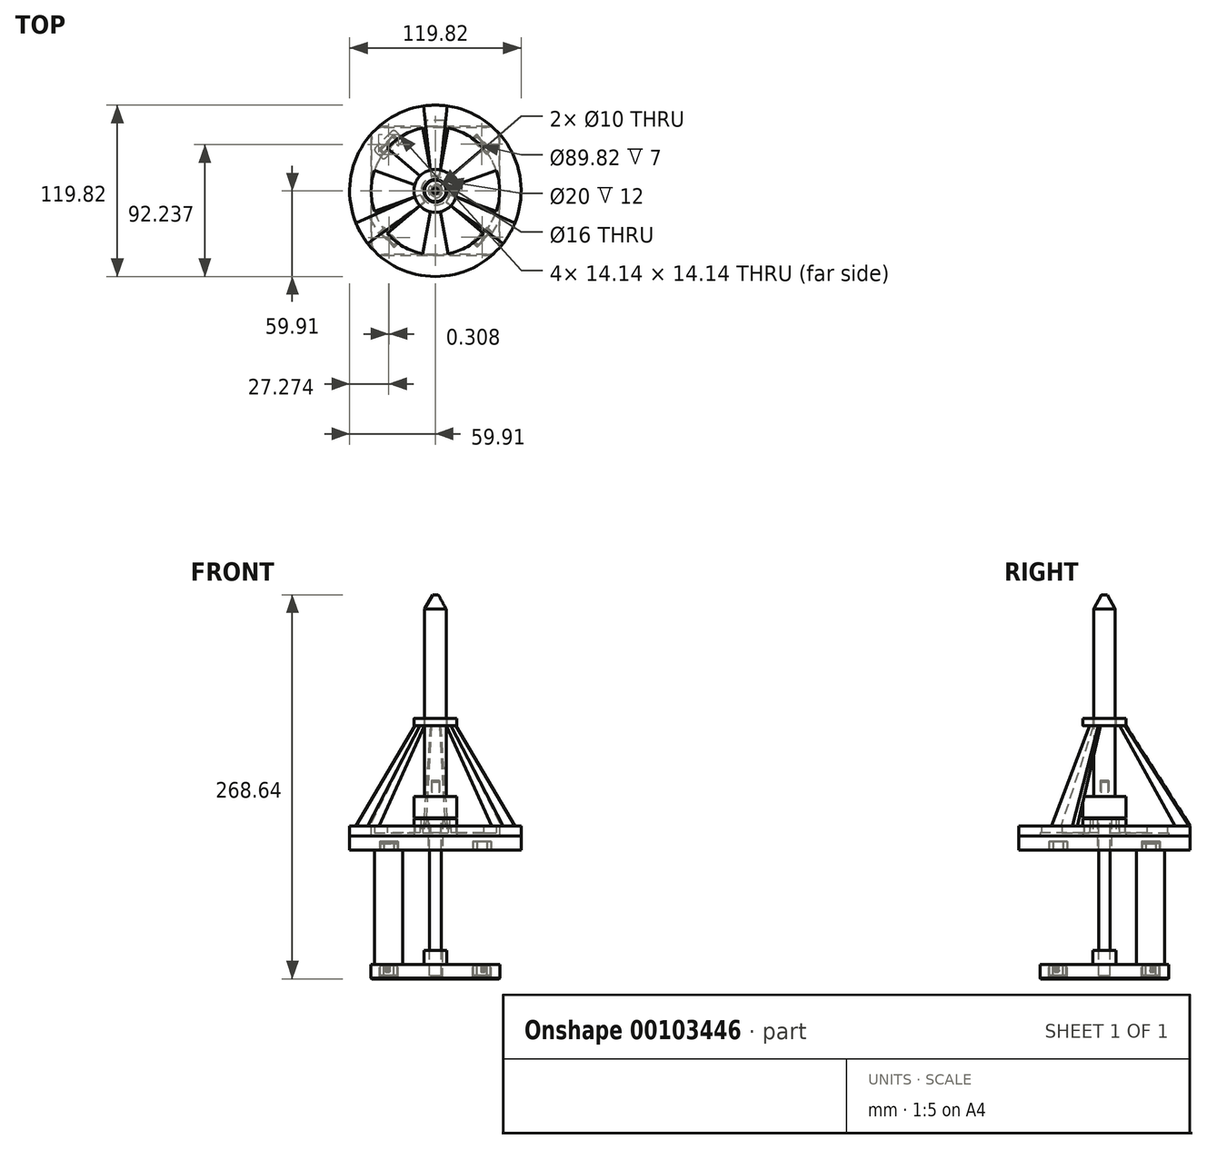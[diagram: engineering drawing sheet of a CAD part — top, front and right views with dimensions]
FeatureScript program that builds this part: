
annotation { "Feature Type Name" : "Feature", "Feature Type Description" : "" }
export const myFeature = defineFeature(function(context is Context, id is Id, definition is map)
    precondition{}
    {
        {
            var Q0;
            Q0=qCreatedBy(makeId("Top.planeOp"),FACE);
            var sketch = newSketch(context, id + "F0", { "sketchPlane" : qUnion([Q0])});
            skLineSegment(sketch, "E0.bottom", {"start": v(36, 45) * mm, "end": v(-36, 45) * mm});
            skLineSegment(sketch, "E0.top", {"start": v(36, -45) * mm, "end": v(-36, -45) * mm});
            skLineSegment(sketch, "E0.left", {"start": v(45, 36) * mm, "end": v(45, -36) * mm});
            skLineSegment(sketch, "E0.right", {"start": v(-45, 36) * mm, "end": v(-45, -36) * mm});
            skPoint(sketch, "E0.middle", {"position": v(0, 0) * mm});
            skPoint(sketch, "E1.visualSharp", {"position": v(-45, 45) * mm});
            skArc(sketch, "E1.filletArc", {"start": v(-36, 45) * mm, "mid": v(-42.36, 42.36) * mm, "end": v(-45, 36) * mm});
            skPoint(sketch, "E2.visualSharp", {"position": v(45, 45) * mm});
            skArc(sketch, "E2.filletArc", {"start": v(45, 36) * mm, "mid": v(42.36, 42.36) * mm, "end": v(36, 45) * mm});
            skPoint(sketch, "E3.visualSharp", {"position": v(45, -45) * mm});
            skArc(sketch, "E3.filletArc", {"start": v(36, -45) * mm, "mid": v(42.36, -42.36) * mm, "end": v(45, -36) * mm});
            skPoint(sketch, "E4.visualSharp", {"position": v(-45, -45) * mm});
            skArc(sketch, "E4.filletArc", {"start": v(-45, -36) * mm, "mid": v(-42.36, -42.36) * mm, "end": v(-36, -45) * mm});
            skCircle(sketch, "E5", {"center": v(0, 0) * mm, "radius": 4 * mm});
            skCircle(sketch, "E6.0", {"center": v(0, 0) * mm, "radius": 5 * mm});
            skLineSegment(sketch, "E7", {"start": v(0, 54.52) * mm, "end": v(0, -60.1) * mm, "construction": true});
            skLineSegment(sketch, "E8", {"start": v(-59, 0) * mm, "end": v(57.8, 0) * mm, "construction": true});
            skLineSegment(sketch, "E9", {"start": v(41.52, 30.51) * mm, "end": v(30.2, 41.83) * mm});
            skLineSegment(sketch, "E10", {"start": v(36, 45) * mm, "end": v(45, 36) * mm, "construction": true});
            skLineSegment(sketch, "E11", {"start": v(27.38, 41.83) * mm, "end": v(23.14, 37.59) * mm});
            skLineSegment(sketch, "E12", {"start": v(23.14, 34.76) * mm, "end": v(34.45, 23.44) * mm});
            skLineSegment(sketch, "E13", {"start": v(37.28, 23.44) * mm, "end": v(41.52, 27.69) * mm});
            skPoint(sketch, "E14.visualSharp", {"position": v(21.72, 36.17) * mm});
            skArc(sketch, "E14.filletArc", {"start": v(23.14, 37.59) * mm, "mid": v(22.55, 36.17) * mm, "end": v(23.14, 34.76) * mm});
            skPoint(sketch, "E15.visualSharp", {"position": v(28.8, 43.24) * mm});
            skArc(sketch, "E15.filletArc", {"start": v(30.2, 41.83) * mm, "mid": v(28.8, 42.41) * mm, "end": v(27.38, 41.83) * mm});
            skPoint(sketch, "E16.visualSharp", {"position": v(42.93, 29.1) * mm});
            skArc(sketch, "E16.filletArc", {"start": v(41.52, 27.69) * mm, "mid": v(42.1, 29.1) * mm, "end": v(41.52, 30.51) * mm});
            skPoint(sketch, "E17.visualSharp", {"position": v(35.86, 22.03) * mm});
            skArc(sketch, "E17.filletArc", {"start": v(34.45, 23.44) * mm, "mid": v(35.86, 22.86) * mm, "end": v(37.28, 23.44) * mm});
            skLineSegment(sketch, "E18.1.0", {"start": v(-41.83, 27.38) * mm, "end": v(-37.59, 23.14) * mm});
            skLineSegment(sketch, "E18.1.1", {"start": v(-34.76, 23.14) * mm, "end": v(-23.44, 34.45) * mm});
            skArc(sketch, "E18.1.2", {"start": v(-27.69, 41.52) * mm, "mid": v(-29.1, 42.1) * mm, "end": v(-30.51, 41.52) * mm});
            skArc(sketch, "E18.1.3", {"start": v(-37.59, 23.14) * mm, "mid": v(-36.17, 22.55) * mm, "end": v(-34.76, 23.14) * mm});
            skPoint(sketch, "E18.1.4", {"position": v(-36.17, 21.72) * mm});
            skPoint(sketch, "E18.1.5", {"position": v(-43.24, 28.8) * mm});
            skLineSegment(sketch, "E18.1.6", {"start": v(-30.51, 41.52) * mm, "end": v(-41.83, 30.2) * mm});
            skArc(sketch, "E18.1.7", {"start": v(-23.44, 34.45) * mm, "mid": v(-22.86, 35.86) * mm, "end": v(-23.44, 37.28) * mm});
            skArc(sketch, "E18.1.8", {"start": v(-41.83, 30.2) * mm, "mid": v(-42.41, 28.8) * mm, "end": v(-41.83, 27.38) * mm});
            skLineSegment(sketch, "E18.1.9", {"start": v(-23.44, 37.28) * mm, "end": v(-27.69, 41.52) * mm});
            skPoint(sketch, "E18.1.10", {"position": v(-22.03, 35.86) * mm});
            skPoint(sketch, "E18.1.11", {"position": v(-29.1, 42.93) * mm});
            skLineSegment(sketch, "E18.2.0", {"start": v(-27.38, -41.83) * mm, "end": v(-23.14, -37.59) * mm});
            skLineSegment(sketch, "E18.2.1", {"start": v(-23.14, -34.76) * mm, "end": v(-34.45, -23.44) * mm});
            skArc(sketch, "E18.2.2", {"start": v(-41.52, -27.69) * mm, "mid": v(-42.1, -29.1) * mm, "end": v(-41.52, -30.51) * mm});
            skArc(sketch, "E18.2.3", {"start": v(-23.14, -37.59) * mm, "mid": v(-22.55, -36.17) * mm, "end": v(-23.14, -34.76) * mm});
            skPoint(sketch, "E18.2.4", {"position": v(-21.72, -36.17) * mm});
            skPoint(sketch, "E18.2.5", {"position": v(-28.8, -43.24) * mm});
            skLineSegment(sketch, "E18.2.6", {"start": v(-41.52, -30.51) * mm, "end": v(-30.2, -41.83) * mm});
            skArc(sketch, "E18.2.7", {"start": v(-34.45, -23.44) * mm, "mid": v(-35.86, -22.86) * mm, "end": v(-37.28, -23.44) * mm});
            skArc(sketch, "E18.2.8", {"start": v(-30.2, -41.83) * mm, "mid": v(-28.8, -42.41) * mm, "end": v(-27.38, -41.83) * mm});
            skLineSegment(sketch, "E18.2.9", {"start": v(-37.28, -23.44) * mm, "end": v(-41.52, -27.69) * mm});
            skPoint(sketch, "E18.2.10", {"position": v(-35.86, -22.03) * mm});
            skPoint(sketch, "E18.2.11", {"position": v(-42.93, -29.1) * mm});
            skLineSegment(sketch, "E18.3.0", {"start": v(41.83, -27.38) * mm, "end": v(37.59, -23.14) * mm});
            skLineSegment(sketch, "E18.3.1", {"start": v(34.76, -23.14) * mm, "end": v(23.44, -34.45) * mm});
            skArc(sketch, "E18.3.2", {"start": v(27.69, -41.52) * mm, "mid": v(29.1, -42.1) * mm, "end": v(30.51, -41.52) * mm});
            skArc(sketch, "E18.3.3", {"start": v(37.59, -23.14) * mm, "mid": v(36.17, -22.55) * mm, "end": v(34.76, -23.14) * mm});
            skPoint(sketch, "E18.3.4", {"position": v(36.17, -21.72) * mm});
            skPoint(sketch, "E18.3.5", {"position": v(43.24, -28.8) * mm});
            skLineSegment(sketch, "E18.3.6", {"start": v(30.51, -41.52) * mm, "end": v(41.83, -30.2) * mm});
            skArc(sketch, "E18.3.7", {"start": v(23.44, -34.45) * mm, "mid": v(22.86, -35.86) * mm, "end": v(23.44, -37.28) * mm});
            skArc(sketch, "E18.3.8", {"start": v(41.83, -30.2) * mm, "mid": v(42.41, -28.8) * mm, "end": v(41.83, -27.38) * mm});
            skLineSegment(sketch, "E18.3.9", {"start": v(23.44, -37.28) * mm, "end": v(27.69, -41.52) * mm});
            skPoint(sketch, "E18.3.10", {"position": v(22.03, -35.86) * mm});
            skPoint(sketch, "E18.3.11", {"position": v(29.1, -42.93) * mm});
            skLineSegment(sketch, "E19.0", {"start": v(-36.17, 25.96) * mm, "end": v(-26.27, 35.86) * mm});
            skLineSegment(sketch, "E19.1", {"start": v(-39, 28.8) * mm, "end": v(-36.17, 25.96) * mm});
            skLineSegment(sketch, "E19.2", {"start": v(-29.1, 38.7) * mm, "end": v(-39, 28.8) * mm});
            skLineSegment(sketch, "E19.3", {"start": v(-26.27, 35.86) * mm, "end": v(-29.1, 38.7) * mm});
            skLineSegment(sketch, "E20.1.0", {"start": v(-35.86, -26.27) * mm, "end": v(-38.7, -29.1) * mm});
            skLineSegment(sketch, "E20.1.1", {"start": v(-38.7, -29.1) * mm, "end": v(-28.8, -39) * mm});
            skLineSegment(sketch, "E20.1.2", {"start": v(-25.96, -36.17) * mm, "end": v(-35.86, -26.27) * mm});
            skLineSegment(sketch, "E20.1.3", {"start": v(-28.8, -39) * mm, "end": v(-25.96, -36.17) * mm});
            skLineSegment(sketch, "E20.2.0", {"start": v(26.27, -35.86) * mm, "end": v(29.1, -38.7) * mm});
            skLineSegment(sketch, "E20.2.1", {"start": v(29.1, -38.7) * mm, "end": v(39, -28.8) * mm});
            skLineSegment(sketch, "E20.2.2", {"start": v(36.17, -25.96) * mm, "end": v(26.27, -35.86) * mm});
            skLineSegment(sketch, "E20.2.3", {"start": v(39, -28.8) * mm, "end": v(36.17, -25.96) * mm});
            skLineSegment(sketch, "E20.3.0", {"start": v(35.86, 26.27) * mm, "end": v(38.7, 29.1) * mm});
            skLineSegment(sketch, "E20.3.1", {"start": v(38.7, 29.1) * mm, "end": v(28.8, 39) * mm});
            skLineSegment(sketch, "E20.3.2", {"start": v(25.96, 36.17) * mm, "end": v(35.86, 26.27) * mm});
            skLineSegment(sketch, "E20.3.3", {"start": v(28.8, 39) * mm, "end": v(25.96, 36.17) * mm});
            skLineSegment(sketch, "E21.0", {"start": v(-29.1, 38.27) * mm, "end": v(-38.58, 28.8) * mm});
            skLineSegment(sketch, "E21.1", {"start": v(-26.7, 35.86) * mm, "end": v(-29.1, 38.27) * mm});
            skLineSegment(sketch, "E21.2", {"start": v(-36.17, 26.39) * mm, "end": v(-26.7, 35.86) * mm});
            skLineSegment(sketch, "E21.3", {"start": v(-38.58, 28.8) * mm, "end": v(-36.17, 26.39) * mm});
            skLineSegment(sketch, "E22.1.0", {"start": v(-38.27, -29.1) * mm, "end": v(-28.8, -38.58) * mm});
            skLineSegment(sketch, "E22.1.1", {"start": v(-28.8, -38.58) * mm, "end": v(-26.39, -36.17) * mm});
            skLineSegment(sketch, "E22.1.2", {"start": v(-26.39, -36.17) * mm, "end": v(-35.86, -26.7) * mm});
            skLineSegment(sketch, "E22.1.3", {"start": v(-35.86, -26.7) * mm, "end": v(-38.27, -29.1) * mm});
            skLineSegment(sketch, "E22.2.0", {"start": v(29.1, -38.27) * mm, "end": v(38.58, -28.8) * mm});
            skLineSegment(sketch, "E22.2.1", {"start": v(38.58, -28.8) * mm, "end": v(36.17, -26.39) * mm});
            skLineSegment(sketch, "E22.2.2", {"start": v(36.17, -26.39) * mm, "end": v(26.7, -35.86) * mm});
            skLineSegment(sketch, "E22.2.3", {"start": v(26.7, -35.86) * mm, "end": v(29.1, -38.27) * mm});
            skLineSegment(sketch, "E22.3.0", {"start": v(38.27, 29.1) * mm, "end": v(28.8, 38.58) * mm});
            skLineSegment(sketch, "E22.3.1", {"start": v(28.8, 38.58) * mm, "end": v(26.39, 36.17) * mm});
            skLineSegment(sketch, "E22.3.2", {"start": v(26.39, 36.17) * mm, "end": v(35.86, 26.7) * mm});
            skLineSegment(sketch, "E22.3.3", {"start": v(35.86, 26.7) * mm, "end": v(38.27, 29.1) * mm});
            skCircle(sketch, "E23.0", {"center": v(0, 0) * mm, "radius": 8 * mm});
            skSolve(sketch);
        }
        {
            var Q0;
            Q0=makeQuery(id+"F0.imprint","IMPRINT",FACE,{"disambiguationData":[TD([[makeQuery(id+"F0.imprint","IMPRINT",EDGE,{"derivedFrom":sQuery(id+"F0.wireOp",EDGE,"E0.bottom")}),1.0]])]});
            var Q1;
            Q1=makeQuery(id+"F0.imprint","IMPRINT",FACE,{"disambiguationData":[TD([[makeQuery(id+"F0.imprint","IMPRINT",EDGE,{"derivedFrom":sQuery(id+"F0.wireOp",EDGE,"E18.1.0")}),1.0]])]});
            var Q2;
            Q2=makeQuery(id+"F0.imprint","IMPRINT",FACE,{"disambiguationData":[TD([[makeQuery(id+"F0.imprint","IMPRINT",EDGE,{"derivedFrom":sQuery(id+"F0.wireOp",EDGE,"E9")}),1.0]])]});
            var Q3;
            Q3=makeQuery(id+"F0.imprint","IMPRINT",FACE,{"disambiguationData":[TD([[makeQuery(id+"F0.imprint","IMPRINT",EDGE,{"derivedFrom":sQuery(id+"F0.wireOp",EDGE,"E18.2.0")}),1.0]])]});
            var Q4;
            Q4=makeQuery(id+"F0.imprint","IMPRINT",FACE,{"disambiguationData":[TD([[makeQuery(id+"F0.imprint","IMPRINT",EDGE,{"derivedFrom":sQuery(id+"F0.wireOp",EDGE,"E18.3.0")}),1.0]])]});
            var Q5;
            Q5=makeQuery(id+"F0.imprint","IMPRINT",FACE,{"disambiguationData":[TD([[makeQuery(id+"F0.imprint","IMPRINT",EDGE,{"derivedFrom":sQuery(id+"F0.wireOp",EDGE,"E6.0")}),-1.0]])]});
            extrude(context, id + "F1", {"entities" : qUnion([Q0, Q1, Q2, Q3, Q4, Q5]), "oppositeDirection" : true, "depth" : 10 * mm});
        }
        {
            var Q0;
            Q0=makeQuery(id+"F0.imprint","IMPRINT",FACE,{"disambiguationData":[TD([[makeQuery(id+"F0.imprint","IMPRINT",EDGE,{"derivedFrom":sQuery(id+"F0.wireOp",EDGE,"E21.0")}),1.0]])]});
            extrude(context, id + "F2", {"entities" : qUnion([Q0]), "oppositeDirection" : true, "depth" : 8 * mm});
        }
        {
            var Q0;
            Q0=makeQuery(id+"F0.imprint","IMPRINT",FACE,{"disambiguationData":[TD([[makeQuery(id+"F0.imprint","IMPRINT",EDGE,{"derivedFrom":sQuery(id+"F0.wireOp",EDGE,"E19.0")}),1.0]])]});
            var Q1;
            Q1=makeQuery(id+"F0.imprint","IMPRINT",FACE,{"disambiguationData":[TD([[makeQuery(id+"F0.imprint","IMPRINT",EDGE,{"derivedFrom":sQuery(id+"F0.wireOp",EDGE,"E21.0")}),1.0]])]});
            var Q2;
            Q2=makeQuery(id+"F0.imprint","IMPRINT",FACE,{"disambiguationData":[TD([[makeQuery(id+"F0.imprint","IMPRINT",EDGE,{"derivedFrom":sQuery(id+"F0.wireOp",EDGE,"E18.1.0")}),1.0]])]});
            extrude(context, id + "F3", {"entities" : qUnion([Q0, Q1, Q2]), "depth" : 80 * mm});
        }
        {
            var Q0;
            Q0=makeQuery(id+"F3.opExtrude","CAP_FACE",FACE,{"disambiguationData":[OSD([sQuery(id+"F0.wireOp",EDGE,"E18.1.0"),sQuery(id+"F0.wireOp",EDGE,"E18.1.1"),sQuery(id+"F0.wireOp",EDGE,"E18.1.2"),sQuery(id+"F0.wireOp",EDGE,"E18.1.3"),sQuery(id+"F0.wireOp",EDGE,"E18.1.6"),sQuery(id+"F0.wireOp",EDGE,"E18.1.7"),sQuery(id+"F0.wireOp",EDGE,"E18.1.8"),sQuery(id+"F0.wireOp",EDGE,"E18.1.9")])],"isStart":false});
            var sketch = newSketch(context, id + "F4", { "sketchPlane" : qUnion([Q0])});
            skLineSegment(sketch, "E24.0", {"start": v(-29.1, 38.27) * mm, "end": v(-38.58, 28.8) * mm});
            skLineSegment(sketch, "E25.0", {"start": v(-26.7, 35.86) * mm, "end": v(-29.1, 38.27) * mm});
            skLineSegment(sketch, "E26.0", {"start": v(-36.17, 26.39) * mm, "end": v(-26.7, 35.86) * mm});
            skLineSegment(sketch, "E27.0", {"start": v(-38.58, 28.8) * mm, "end": v(-36.17, 26.39) * mm});
            skSolve(sketch);
        }
        {
            var Q0;
            Q0=makeQuery(id+"F4.imprint","IMPRINT",FACE,{"disambiguationData":[TD([[makeQuery(id+"F4.imprint","IMPRINT",EDGE,{"derivedFrom":sQuery(id+"F4.wireOp",EDGE,"E24.0")}),1.0]])]});
            extrude(context, id + "F5", {"entities" : qUnion([Q0]), "operationType" : NewBodyOperationType.ADD, "depth" : 5 * mm});
        }
        {
            var Q0;
            Q0=makeQuery(id+"F2.opExtrude","CAP_FACE",FACE,{"disambiguationData":[OSD([sQuery(id+"F0.wireOp",EDGE,"E21.0"),sQuery(id+"F0.wireOp",EDGE,"E21.1"),sQuery(id+"F0.wireOp",EDGE,"E21.2"),sQuery(id+"F0.wireOp",EDGE,"E21.3")])],"isStart":false});
            var Q1;
            Q1=makeQuery(id+"F5.opExtrude","CAP_FACE",FACE,{"disambiguationData":[OSD([sQuery(id+"F4.wireOp",EDGE,"E24.0"),sQuery(id+"F4.wireOp",EDGE,"E25.0"),sQuery(id+"F4.wireOp",EDGE,"E26.0"),sQuery(id+"F4.wireOp",EDGE,"E27.0")])],"isStart":false});
            chamfer(context, id + "F6", {"entities" : qUnion([Q0, Q1]), "width" : .5 * mm, "tangentPropagation" : true});
        }
        {
            var Q0;
            Q0=makeQuery(id+"F2.opExtrude","SWEPT_FACE",FACE,{"disambiguationData":[OSD([sQuery(id+"F0.wireOp",EDGE,"E21.0")])]});
            var sketch = newSketch(context, id + "F7", { "sketchPlane" : qUnion([Q0])});
            skText(sketch, "E28", { "text": "B", "fontName": "OpenSans-Regular.ttf"});
            const initialGuessF7  = {"E28": [-0.00182, -0.00547, 1, 0, 0.00441]};
            skSetInitialGuess(sketch, initialGuessF7);
            skSolve(sketch);
        }
        {
            var Q0;
            Q0=makeQuery(id+"F7.imprint","IMPRINT",FACE,{"disambiguationData":[TD([[makeQuery(id+"F7.imprint","IMPRINT",EDGE,{"derivedFrom":sQuery(id+"F7.wireOp",EDGE,"E28.sketch_text.stroke-0")}),-1.0]])]});
            extrude(context, id + "F8", {"entities" : qUnion([Q0]), "operationType" : NewBodyOperationType.REMOVE, "oppositeDirection" : true, "depth" : 1 * mm});
        }
        {
            var Q0;
            Q0=makeQuery(id+"F2.opExtrude","SWEPT_BODY",BODY,{"disambiguationData":[OSD([sQuery(id+"F0.wireOp",EDGE,"E21.0"),sQuery(id+"F0.wireOp",EDGE,"E21.1"),sQuery(id+"F0.wireOp",EDGE,"E21.2"),sQuery(id+"F0.wireOp",EDGE,"E21.3")])]});
            var Q1;
            Q1=makeQuery(id+"F1.opExtrude","SWEPT_FACE",FACE,{"disambiguationData":[OSD([sQuery(id+"F0.wireOp",EDGE,"E6.0")])]});
            circularPattern(context, id + "F9", {"entities" : qUnion([Q0]), "axis" : qUnion([Q1]), "angle" : 90 * degree, "instanceCount" : 4});
        }
        {
            var Q0;
            Q0=makeQuery(id+"F3.opExtrude","CAP_FACE",FACE,{"disambiguationData":[OSD([sQuery(id+"F0.wireOp",EDGE,"E18.1.0"),sQuery(id+"F0.wireOp",EDGE,"E18.1.1"),sQuery(id+"F0.wireOp",EDGE,"E18.1.2"),sQuery(id+"F0.wireOp",EDGE,"E18.1.3"),sQuery(id+"F0.wireOp",EDGE,"E18.1.6"),sQuery(id+"F0.wireOp",EDGE,"E18.1.7"),sQuery(id+"F0.wireOp",EDGE,"E18.1.8"),sQuery(id+"F0.wireOp",EDGE,"E18.1.9")])],"isStart":false});
            var sketch = newSketch(context, id + "F10", { "sketchPlane" : qUnion([Q0])});
            skLineSegment(sketch, "E29.0", {"start": v(-26.27, 35.86) * mm, "end": v(-29.1, 38.7) * mm});
            skLineSegment(sketch, "E30.0", {"start": v(-36.17, 25.96) * mm, "end": v(-26.27, 35.86) * mm});
            skLineSegment(sketch, "E31.0", {"start": v(-29.1, 38.7) * mm, "end": v(-39, 28.8) * mm});
            skLineSegment(sketch, "E32.0", {"start": v(-39, 28.8) * mm, "end": v(-36.17, 25.96) * mm});
            skLineSegment(sketch, "E33.0", {"start": v(38.7, 29.1) * mm, "end": v(28.8, 39) * mm});
            skLineSegment(sketch, "E34.0", {"start": v(28.8, 39) * mm, "end": v(25.96, 36.17) * mm});
            skLineSegment(sketch, "E35.0", {"start": v(25.96, 36.17) * mm, "end": v(35.86, 26.27) * mm});
            skLineSegment(sketch, "E36.0", {"start": v(35.86, 26.27) * mm, "end": v(38.7, 29.1) * mm});
            skLineSegment(sketch, "E37.0", {"start": v(39, -28.8) * mm, "end": v(36.17, -25.96) * mm});
            skLineSegment(sketch, "E38.0", {"start": v(36.17, -25.96) * mm, "end": v(26.27, -35.86) * mm});
            skLineSegment(sketch, "E39.0", {"start": v(29.1, -38.7) * mm, "end": v(39, -28.8) * mm});
            skLineSegment(sketch, "E40.0", {"start": v(26.27, -35.86) * mm, "end": v(29.1, -38.7) * mm});
            skLineSegment(sketch, "E41.0", {"start": v(-25.96, -36.17) * mm, "end": v(-35.86, -26.27) * mm});
            skLineSegment(sketch, "E42.0", {"start": v(-35.86, -26.27) * mm, "end": v(-38.7, -29.1) * mm});
            skLineSegment(sketch, "E43.0", {"start": v(-38.7, -29.1) * mm, "end": v(-28.8, -39) * mm});
            skLineSegment(sketch, "E44.0", {"start": v(-28.8, -39) * mm, "end": v(-25.96, -36.17) * mm});
            skCircle(sketch, "E45", {"center": v(0, 0) * mm, "radius": 59.91 * mm});
            skArc(sketch, "E46.0", {"start": v(45, 36) * mm, "mid": v(42.36, 42.36) * mm, "end": v(36, 45) * mm, "construction": true});
            skCircle(sketch, "E47.0", {"center": v(0, 0) * mm, "radius": 5 * mm});
            skSolve(sketch);
        }
        {
            var Q0;
            Q0 = qSketchRegion(id + "F10", true);
            extrude(context, id + "F11", {"entities" : qUnion([Q0]), "depth" : 10 * mm});
        }
        {
            var Q0;
            Q0=makeQuery(id+"F11.opExtrude","CAP_FACE",FACE,{"disambiguationData":[OSD([sQuery(id+"F10.wireOp",EDGE,"E29.0"),sQuery(id+"F10.wireOp",EDGE,"E30.0"),sQuery(id+"F10.wireOp",EDGE,"E31.0"),sQuery(id+"F10.wireOp",EDGE,"E32.0"),sQuery(id+"F10.wireOp",EDGE,"E33.0"),sQuery(id+"F10.wireOp",EDGE,"E34.0"),sQuery(id+"F10.wireOp",EDGE,"E35.0"),sQuery(id+"F10.wireOp",EDGE,"E36.0"),sQuery(id+"F10.wireOp",EDGE,"E37.0"),sQuery(id+"F10.wireOp",EDGE,"E38.0"),sQuery(id+"F10.wireOp",EDGE,"E39.0"),sQuery(id+"F10.wireOp",EDGE,"E40.0"),sQuery(id+"F10.wireOp",EDGE,"E41.0"),sQuery(id+"F10.wireOp",EDGE,"E42.0"),sQuery(id+"F10.wireOp",EDGE,"E43.0"),sQuery(id+"F10.wireOp",EDGE,"E44.0"),sQuery(id+"F10.wireOp",EDGE,"E45"),sQuery(id+"F10.wireOp",EDGE,"E47.0")])],"isStart":false});
            var sketch = newSketch(context, id + "F12", { "sketchPlane" : qUnion([Q0])});
            skCircle(sketch, "E48.0.0", {"center": v(0, 0) * mm, "radius": 59.91 * mm});
            skLineSegment(sketch, "E49.0", {"start": v(-36.17, 25.96) * mm, "end": v(-26.27, 35.86) * mm});
            skLineSegment(sketch, "E50.0", {"start": v(-39, 28.8) * mm, "end": v(-36.17, 25.96) * mm});
            skLineSegment(sketch, "E51.0", {"start": v(-29.1, 38.7) * mm, "end": v(-39, 28.8) * mm});
            skLineSegment(sketch, "E52.0", {"start": v(-26.27, 35.86) * mm, "end": v(-29.1, 38.7) * mm});
            skLineSegment(sketch, "E53.0", {"start": v(38.7, 29.1) * mm, "end": v(28.8, 39) * mm});
            skLineSegment(sketch, "E54.0", {"start": v(28.8, 39) * mm, "end": v(25.96, 36.17) * mm});
            skLineSegment(sketch, "E55.0", {"start": v(25.96, 36.17) * mm, "end": v(35.86, 26.27) * mm});
            skLineSegment(sketch, "E56.0", {"start": v(35.86, 26.27) * mm, "end": v(38.7, 29.1) * mm});
            skLineSegment(sketch, "E57.0", {"start": v(29.1, -38.7) * mm, "end": v(39, -28.8) * mm});
            skLineSegment(sketch, "E58.0", {"start": v(39, -28.8) * mm, "end": v(36.17, -25.96) * mm});
            skLineSegment(sketch, "E59.0", {"start": v(36.17, -25.96) * mm, "end": v(26.27, -35.86) * mm});
            skLineSegment(sketch, "E60.0", {"start": v(26.27, -35.86) * mm, "end": v(29.1, -38.7) * mm});
            skLineSegment(sketch, "E61.0", {"start": v(-25.96, -36.17) * mm, "end": v(-35.86, -26.27) * mm});
            skLineSegment(sketch, "E62.0", {"start": v(-35.86, -26.27) * mm, "end": v(-38.7, -29.1) * mm});
            skLineSegment(sketch, "E63.0", {"start": v(-38.7, -29.1) * mm, "end": v(-28.8, -39) * mm});
            skLineSegment(sketch, "E64.0", {"start": v(-28.8, -39) * mm, "end": v(-25.96, -36.17) * mm});
            skSolve(sketch);
        }
        {
            var Q0;
            Q0=makeQuery(id+"F12.imprint","IMPRINT",FACE,{"disambiguationData":[TD([[makeQuery(id+"F12.imprint","IMPRINT",EDGE,{"derivedFrom":sQuery(id+"F12.wireOp",EDGE,"E57.0")}),1.0]])]});
            var Q1;
            Q1=makeQuery(id+"F12.imprint","IMPRINT",FACE,{"disambiguationData":[TD([[makeQuery(id+"F12.imprint","IMPRINT",EDGE,{"derivedFrom":sQuery(id+"F12.wireOp",EDGE,"E53.0")}),1.0]])]});
            var Q2;
            Q2=makeQuery(id+"F12.imprint","IMPRINT",FACE,{"disambiguationData":[TD([[makeQuery(id+"F12.imprint","IMPRINT",EDGE,{"derivedFrom":sQuery(id+"F12.wireOp",EDGE,"E49.0")}),1.0]])]});
            var Q3;
            Q3=makeQuery(id+"F12.imprint","IMPRINT",FACE,{"disambiguationData":[TD([[makeQuery(id+"F12.imprint","IMPRINT",EDGE,{"derivedFrom":sQuery(id+"F12.wireOp",EDGE,"E61.0")}),1.0]])]});
            extrude(context, id + "F13", {"entities" : qUnion([Q0, Q1, Q2, Q3]), "operationType" : NewBodyOperationType.ADD, "oppositeDirection" : true, "depth" : 4 * mm});
        }
        {
            var Q0;
            Q0=makeQuery(id+"F1.opExtrude","CAP_EDGE",EDGE,{"disambiguationData":[OSD([sQuery(id+"F0.wireOp",EDGE,"E20.1.2")])],"isStart":true});
            var Q1;
            Q1=makeQuery(id+"F1.opExtrude","CAP_EDGE",EDGE,{"disambiguationData":[OSD([sQuery(id+"F0.wireOp",EDGE,"E20.1.0")])],"isStart":true});
            var Q2;
            Q2=makeQuery(id+"F1.opExtrude","CAP_EDGE",EDGE,{"disambiguationData":[OSD([sQuery(id+"F0.wireOp",EDGE,"E20.1.1")])],"isStart":true});
            var Q3;
            Q3=makeQuery(id+"F1.opExtrude","CAP_EDGE",EDGE,{"disambiguationData":[OSD([sQuery(id+"F0.wireOp",EDGE,"E20.1.3")])],"isStart":true});
            var Q4;
            Q4=makeQuery(id+"F1.opExtrude","CAP_EDGE",EDGE,{"disambiguationData":[OSD([sQuery(id+"F0.wireOp",EDGE,"E20.2.2")])],"isStart":true});
            var Q5;
            Q5=makeQuery(id+"F1.opExtrude","CAP_EDGE",EDGE,{"disambiguationData":[OSD([sQuery(id+"F0.wireOp",EDGE,"E20.2.0")])],"isStart":true});
            var Q6;
            Q6=makeQuery(id+"F1.opExtrude","CAP_EDGE",EDGE,{"disambiguationData":[OSD([sQuery(id+"F0.wireOp",EDGE,"E20.2.1")])],"isStart":true});
            var Q7;
            Q7=makeQuery(id+"F1.opExtrude","CAP_EDGE",EDGE,{"disambiguationData":[OSD([sQuery(id+"F0.wireOp",EDGE,"E20.2.3")])],"isStart":true});
            var Q8;
            Q8=makeQuery(id+"F1.opExtrude","CAP_EDGE",EDGE,{"disambiguationData":[OSD([sQuery(id+"F0.wireOp",EDGE,"E20.3.2")])],"isStart":true});
            var Q9;
            Q9=makeQuery(id+"F1.opExtrude","CAP_EDGE",EDGE,{"disambiguationData":[OSD([sQuery(id+"F0.wireOp",EDGE,"E20.3.0")])],"isStart":true});
            var Q10;
            Q10=makeQuery(id+"F1.opExtrude","CAP_EDGE",EDGE,{"disambiguationData":[OSD([sQuery(id+"F0.wireOp",EDGE,"E20.3.1")])],"isStart":true});
            var Q11;
            Q11=makeQuery(id+"F1.opExtrude","CAP_EDGE",EDGE,{"disambiguationData":[OSD([sQuery(id+"F0.wireOp",EDGE,"E20.3.3")])],"isStart":true});
            var Q12;
            Q12=makeQuery(id+"F1.opExtrude","CAP_EDGE",EDGE,{"disambiguationData":[OSD([sQuery(id+"F0.wireOp",EDGE,"E19.0")])],"isStart":true});
            var Q13;
            Q13=makeQuery(id+"F1.opExtrude","CAP_EDGE",EDGE,{"disambiguationData":[OSD([sQuery(id+"F0.wireOp",EDGE,"E19.2")])],"isStart":true});
            var Q14;
            Q14=makeQuery(id+"F1.opExtrude","CAP_EDGE",EDGE,{"disambiguationData":[OSD([sQuery(id+"F0.wireOp",EDGE,"E19.1")])],"isStart":true});
            var Q15;
            Q15=makeQuery(id+"F1.opExtrude","CAP_EDGE",EDGE,{"disambiguationData":[OSD([sQuery(id+"F0.wireOp",EDGE,"E19.3")])],"isStart":true});
            var Q16;
            Q16=makeQuery(id+"F11.opExtrude","CAP_EDGE",EDGE,{"disambiguationData":[OSD([sQuery(id+"F10.wireOp",EDGE,"E30.0")])],"isStart":true});
            var Q17;
            Q17=makeQuery(id+"F11.opExtrude","CAP_EDGE",EDGE,{"disambiguationData":[OSD([sQuery(id+"F10.wireOp",EDGE,"E31.0")])],"isStart":true});
            var Q18;
            Q18=makeQuery(id+"F11.opExtrude","CAP_EDGE",EDGE,{"disambiguationData":[OSD([sQuery(id+"F10.wireOp",EDGE,"E29.0")])],"isStart":true});
            var Q19;
            Q19=makeQuery(id+"F11.opExtrude","CAP_EDGE",EDGE,{"disambiguationData":[OSD([sQuery(id+"F10.wireOp",EDGE,"E32.0")])],"isStart":true});
            var Q20;
            Q20=makeQuery(id+"F11.opExtrude","CAP_EDGE",EDGE,{"disambiguationData":[OSD([sQuery(id+"F10.wireOp",EDGE,"E41.0")])],"isStart":true});
            var Q21;
            Q21=makeQuery(id+"F11.opExtrude","CAP_EDGE",EDGE,{"disambiguationData":[OSD([sQuery(id+"F10.wireOp",EDGE,"E43.0")])],"isStart":true});
            var Q22;
            Q22=makeQuery(id+"F11.opExtrude","CAP_EDGE",EDGE,{"disambiguationData":[OSD([sQuery(id+"F10.wireOp",EDGE,"E42.0")])],"isStart":true});
            var Q23;
            Q23=makeQuery(id+"F11.opExtrude","CAP_EDGE",EDGE,{"disambiguationData":[OSD([sQuery(id+"F10.wireOp",EDGE,"E44.0")])],"isStart":true});
            var Q24;
            Q24=makeQuery(id+"F11.opExtrude","CAP_EDGE",EDGE,{"disambiguationData":[OSD([sQuery(id+"F10.wireOp",EDGE,"E39.0")])],"isStart":true});
            var Q25;
            Q25=makeQuery(id+"F11.opExtrude","CAP_EDGE",EDGE,{"disambiguationData":[OSD([sQuery(id+"F10.wireOp",EDGE,"E37.0")])],"isStart":true});
            var Q26;
            Q26=makeQuery(id+"F11.opExtrude","CAP_EDGE",EDGE,{"disambiguationData":[OSD([sQuery(id+"F10.wireOp",EDGE,"E38.0")])],"isStart":true});
            var Q27;
            Q27=makeQuery(id+"F11.opExtrude","CAP_EDGE",EDGE,{"disambiguationData":[OSD([sQuery(id+"F10.wireOp",EDGE,"E40.0")])],"isStart":true});
            var Q28;
            Q28=makeQuery(id+"F11.opExtrude","CAP_EDGE",EDGE,{"disambiguationData":[OSD([sQuery(id+"F10.wireOp",EDGE,"E33.0")])],"isStart":true});
            var Q29;
            Q29=makeQuery(id+"F11.opExtrude","CAP_EDGE",EDGE,{"disambiguationData":[OSD([sQuery(id+"F10.wireOp",EDGE,"E36.0")])],"isStart":true});
            var Q30;
            Q30=makeQuery(id+"F11.opExtrude","CAP_EDGE",EDGE,{"disambiguationData":[OSD([sQuery(id+"F10.wireOp",EDGE,"E35.0")])],"isStart":true});
            var Q31;
            Q31=makeQuery(id+"F11.opExtrude","CAP_EDGE",EDGE,{"disambiguationData":[OSD([sQuery(id+"F10.wireOp",EDGE,"E34.0")])],"isStart":true});
            var Q32;
            Q32=makeQuery(id+"F1.opExtrude","CAP_EDGE",EDGE,{"disambiguationData":[OSD([sQuery(id+"F0.wireOp",EDGE,"E20.2.1")])],"isStart":false});
            var Q33;
            Q33=makeQuery(id+"F1.opExtrude","CAP_EDGE",EDGE,{"disambiguationData":[OSD([sQuery(id+"F0.wireOp",EDGE,"E20.2.3")])],"isStart":false});
            var Q34;
            Q34=makeQuery(id+"F1.opExtrude","CAP_EDGE",EDGE,{"disambiguationData":[OSD([sQuery(id+"F0.wireOp",EDGE,"E20.2.2")])],"isStart":false});
            var Q35;
            Q35=makeQuery(id+"F1.opExtrude","CAP_EDGE",EDGE,{"disambiguationData":[OSD([sQuery(id+"F0.wireOp",EDGE,"E20.2.0")])],"isStart":false});
            var Q36;
            Q36=makeQuery(id+"F1.opExtrude","CAP_EDGE",EDGE,{"disambiguationData":[OSD([sQuery(id+"F0.wireOp",EDGE,"E20.3.1")])],"isStart":false});
            var Q37;
            Q37=makeQuery(id+"F1.opExtrude","CAP_EDGE",EDGE,{"disambiguationData":[OSD([sQuery(id+"F0.wireOp",EDGE,"E20.3.0")])],"isStart":false});
            var Q38;
            Q38=makeQuery(id+"F1.opExtrude","CAP_EDGE",EDGE,{"disambiguationData":[OSD([sQuery(id+"F0.wireOp",EDGE,"E20.3.2")])],"isStart":false});
            var Q39;
            Q39=makeQuery(id+"F1.opExtrude","CAP_EDGE",EDGE,{"disambiguationData":[OSD([sQuery(id+"F0.wireOp",EDGE,"E20.3.3")])],"isStart":false});
            var Q40;
            Q40=makeQuery(id+"F1.opExtrude","CAP_EDGE",EDGE,{"disambiguationData":[OSD([sQuery(id+"F0.wireOp",EDGE,"E20.1.2")])],"isStart":false});
            var Q41;
            Q41=makeQuery(id+"F1.opExtrude","CAP_EDGE",EDGE,{"disambiguationData":[OSD([sQuery(id+"F0.wireOp",EDGE,"E20.1.3")])],"isStart":false});
            var Q42;
            Q42=makeQuery(id+"F1.opExtrude","CAP_EDGE",EDGE,{"disambiguationData":[OSD([sQuery(id+"F0.wireOp",EDGE,"E20.1.1")])],"isStart":false});
            var Q43;
            Q43=makeQuery(id+"F1.opExtrude","CAP_EDGE",EDGE,{"disambiguationData":[OSD([sQuery(id+"F0.wireOp",EDGE,"E20.1.0")])],"isStart":false});
            var Q44;
            Q44=makeQuery(id+"F1.opExtrude","CAP_EDGE",EDGE,{"disambiguationData":[OSD([sQuery(id+"F0.wireOp",EDGE,"E19.0")])],"isStart":false});
            var Q45;
            Q45=makeQuery(id+"F1.opExtrude","CAP_EDGE",EDGE,{"disambiguationData":[OSD([sQuery(id+"F0.wireOp",EDGE,"E19.3")])],"isStart":false});
            var Q46;
            Q46=makeQuery(id+"F1.opExtrude","CAP_EDGE",EDGE,{"disambiguationData":[OSD([sQuery(id+"F0.wireOp",EDGE,"E19.2")])],"isStart":false});
            var Q47;
            Q47=makeQuery(id+"F1.opExtrude","CAP_EDGE",EDGE,{"disambiguationData":[OSD([sQuery(id+"F0.wireOp",EDGE,"E19.1")])],"isStart":false});
            var Q48;
            Q48=makeQuery(id+"F1.opExtrude","CAP_EDGE",EDGE,{"disambiguationData":[OSD([sQuery(id+"F0.wireOp",EDGE,"E0.right")])],"isStart":false});
            chamfer(context, id + "F14", {"entities" : qUnion([Q0, Q1, Q2, Q3, Q4, Q5, Q6, Q7, Q8, Q9, Q10, Q11, Q12, Q13, Q14, Q15, Q16, Q17, Q18, Q19, Q20, Q21, Q22, Q23, Q24, Q25, Q26, Q27, Q28, Q29, Q30, Q31, Q32, Q33, Q34, Q35, Q36, Q37, Q38, Q39, Q40, Q41, Q42, Q43, Q44, Q45, Q46, Q47, Q48]), "width" : .5 * mm, "tangentPropagation" : true});
        }
        {
            var Q0;
            Q0=makeQuery(id+"F13.boolean.opBoolean","MERGE",FACE,{"derivedFrom":[makeQuery(id+"F11.opExtrude","CAP_FACE",FACE,{"disambiguationData":[OSD([sQuery(id+"F10.wireOp",EDGE,"E29.0"),sQuery(id+"F10.wireOp",EDGE,"E30.0"),sQuery(id+"F10.wireOp",EDGE,"E31.0"),sQuery(id+"F10.wireOp",EDGE,"E32.0"),sQuery(id+"F10.wireOp",EDGE,"E33.0"),sQuery(id+"F10.wireOp",EDGE,"E34.0"),sQuery(id+"F10.wireOp",EDGE,"E35.0"),sQuery(id+"F10.wireOp",EDGE,"E36.0"),sQuery(id+"F10.wireOp",EDGE,"E37.0"),sQuery(id+"F10.wireOp",EDGE,"E38.0"),sQuery(id+"F10.wireOp",EDGE,"E39.0"),sQuery(id+"F10.wireOp",EDGE,"E40.0"),sQuery(id+"F10.wireOp",EDGE,"E41.0"),sQuery(id+"F10.wireOp",EDGE,"E42.0"),sQuery(id+"F10.wireOp",EDGE,"E43.0"),sQuery(id+"F10.wireOp",EDGE,"E44.0"),sQuery(id+"F10.wireOp",EDGE,"E45"),sQuery(id+"F10.wireOp",EDGE,"E47.0")])],"isStart":false}),makeQuery(id+"F13.opExtrude","CAP_FACE",FACE,{"disambiguationData":[OSD([sQuery(id+"F12.wireOp",EDGE,"E49.0"),sQuery(id+"F12.wireOp",EDGE,"E50.0"),sQuery(id+"F12.wireOp",EDGE,"E51.0"),sQuery(id+"F12.wireOp",EDGE,"E52.0")])],"isStart":true}),makeQuery(id+"F13.opExtrude","CAP_FACE",FACE,{"disambiguationData":[OSD([sQuery(id+"F12.wireOp",EDGE,"E53.0"),sQuery(id+"F12.wireOp",EDGE,"E54.0"),sQuery(id+"F12.wireOp",EDGE,"E55.0"),sQuery(id+"F12.wireOp",EDGE,"E56.0")])],"isStart":true}),makeQuery(id+"F13.opExtrude","CAP_FACE",FACE,{"disambiguationData":[OSD([sQuery(id+"F12.wireOp",EDGE,"E57.0"),sQuery(id+"F12.wireOp",EDGE,"E58.0"),sQuery(id+"F12.wireOp",EDGE,"E59.0"),sQuery(id+"F12.wireOp",EDGE,"E60.0")])],"isStart":true}),makeQuery(id+"F13.opExtrude","CAP_FACE",FACE,{"disambiguationData":[OSD([sQuery(id+"F12.wireOp",EDGE,"E61.0"),sQuery(id+"F12.wireOp",EDGE,"E62.0"),sQuery(id+"F12.wireOp",EDGE,"E63.0"),sQuery(id+"F12.wireOp",EDGE,"E64.0")])],"isStart":true})]});
            var sketch = newSketch(context, id + "F15", { "sketchPlane" : qUnion([Q0])});
            skCircle(sketch, "E65.0", {"center": v(0, 0) * mm, "radius": 59.91 * mm});
            skCircle(sketch, "E66.0", {"center": v(0, 0) * mm, "radius": 5 * mm});
            skArc(sketch, "E67.0", {"start": v(-8.95, 44.01) * mm, "mid": v(-22.46, 38.9) * mm, "end": v(-33.64, 29.76) * mm});
            skArc(sketch, "E68.0", {"start": v(-3.63, 14.55) * mm, "mid": v(-7.5, 13) * mm, "end": v(-10.8, 10.42) * mm});
            skLineSegment(sketch, "E69", {"start": v(0, 74.9) * mm, "end": v(0, -85.15) * mm, "construction": true});
            skLineSegment(sketch, "E70", {"start": v(-3.63, 14.55) * mm, "end": v(-8.95, 44.01) * mm});
            skLineSegment(sketch, "E71.MirrorCS", {"start": v(3.63, 14.55) * mm, "end": v(8.95, 44.01) * mm});
            skLineSegment(sketch, "E72.1.0", {"start": v(-14.42, 4.14) * mm, "end": v(-42.59, 14.25) * mm});
            skLineSegment(sketch, "E72.1.1", {"start": v(-10.8, 10.42) * mm, "end": v(-33.64, 29.76) * mm});
            skLineSegment(sketch, "E72.2.0", {"start": v(-10.8, -10.42) * mm, "end": v(-33.64, -29.76) * mm});
            skLineSegment(sketch, "E72.2.1", {"start": v(-14.42, -4.14) * mm, "end": v(-42.59, -14.25) * mm});
            skLineSegment(sketch, "E72.3.0", {"start": v(3.63, -14.55) * mm, "end": v(8.95, -44.01) * mm});
            skLineSegment(sketch, "E72.3.1", {"start": v(-3.63, -14.55) * mm, "end": v(-8.95, -44.01) * mm});
            skLineSegment(sketch, "E72.4.0", {"start": v(14.42, -4.14) * mm, "end": v(42.59, -14.25) * mm});
            skLineSegment(sketch, "E72.4.1", {"start": v(10.8, -10.42) * mm, "end": v(33.64, -29.76) * mm});
            skLineSegment(sketch, "E72.5.0", {"start": v(10.8, 10.42) * mm, "end": v(33.64, 29.76) * mm});
            skLineSegment(sketch, "E72.5.1", {"start": v(14.42, 4.14) * mm, "end": v(42.59, 14.25) * mm});
            skCircle(sketch, "E73.0", {"center": v(0, 0) * mm, "radius": 8 * mm});
            skArc(sketch, "E74.trimOffspring", {"start": v(-42.59, 14.25) * mm, "mid": v(-44.91, 0) * mm, "end": v(-42.59, -14.25) * mm});
            skArc(sketch, "E75.trimOffspring", {"start": v(-14.42, 4.14) * mm, "mid": v(-15, 0) * mm, "end": v(-14.42, -4.14) * mm});
            skArc(sketch, "E76.trimOffspring", {"start": v(-10.8, -10.42) * mm, "mid": v(-7.5, -13) * mm, "end": v(-3.63, -14.55) * mm});
            skArc(sketch, "E77.trimOffspring", {"start": v(-33.64, -29.76) * mm, "mid": v(-22.46, -38.9) * mm, "end": v(-8.95, -44.01) * mm});
            skArc(sketch, "E78.trimOffspring", {"start": v(8.95, -44.01) * mm, "mid": v(22.46, -38.9) * mm, "end": v(33.64, -29.76) * mm});
            skArc(sketch, "E79.trimOffspring", {"start": v(3.63, -14.55) * mm, "mid": v(7.5, -13) * mm, "end": v(10.8, -10.42) * mm});
            skArc(sketch, "E80.trimOffspring", {"start": v(14.42, -4.14) * mm, "mid": v(15, 0) * mm, "end": v(14.42, 4.14) * mm});
            skArc(sketch, "E81.trimOffspring", {"start": v(42.59, -14.25) * mm, "mid": v(44.91, 0) * mm, "end": v(42.59, 14.25) * mm});
            skArc(sketch, "E82.trimOffspring", {"start": v(33.64, 29.76) * mm, "mid": v(22.46, 38.9) * mm, "end": v(8.95, 44.01) * mm});
            skArc(sketch, "E83.trimOffspring", {"start": v(10.8, 10.42) * mm, "mid": v(7.5, 13) * mm, "end": v(3.63, 14.55) * mm});
            skCircle(sketch, "E84.0", {"center": v(0, 0) * mm, "radius": 10 * mm});
            skCircle(sketch, "E85", {"center": v(0, 0) * mm, "radius": 44.91 * mm});
            skCircle(sketch, "E86", {"center": v(0, 0) * mm, "radius": 15 * mm});
            skCircle(sketch, "E87", {"center": v(0, 0) * mm, "radius": 4 * mm});
            skSolve(sketch);
        }
        {
            var Q0;
            Q0=makeQuery(id+"F15.imprint","IMPRINT",FACE,{"disambiguationData":[TD([[makeQuery(id+"F15.imprint","IMPRINT",EDGE,{"derivedFrom":sQuery(id+"F15.wireOp",EDGE,"E66.0")}),-1.0]])]});
            extrude(context, id + "F16", {"entities" : qUnion([Q0]), "operationType" : NewBodyOperationType.ADD, "depth" : 12 * mm});
        }
        {
            var Q0;
            Q0=makeQuery(id+"F15.imprint","IMPRINT",FACE,{"disambiguationData":[TD([[makeQuery(id+"F15.imprint","IMPRINT",EDGE,{"derivedFrom":sQuery(id+"F15.wireOp",EDGE,"E65.0")}),1.0]])]});
            var Q1;
            Q1=makeQuery(id+"F15.imprint","IMPRINT",FACE,{"disambiguationData":[TD([[makeQuery(id+"F15.imprint","IMPRINT",EDGE,{"derivedFrom":sQuery(id+"F15.wireOp",EDGE,"E84.0")}),-1.0]])]});
            extrude(context, id + "F17", {"entities" : qUnion([Q0, Q1]), "depth" : 2 * mm});
        }
        {
            var Q0;
            Q0=makeQuery(id+"F17.opExtrude","CAP_FACE",FACE,{"disambiguationData":[OSD([sQuery(id+"F15.wireOp",EDGE,"E65.0"),sQuery(id+"F15.wireOp",EDGE,"E85")])],"isStart":false});
            var sketch = newSketch(context, id + "F18", { "sketchPlane" : qUnion([Q0])});
            skCircle(sketch, "E88.0", {"center": v(0, 0) * mm, "radius": 44.91 * mm});
            skCircle(sketch, "E89.0", {"center": v(0, 0) * mm, "radius": 59.91 * mm});
            skLineSegment(sketch, "E90.0.0", {"start": v(-33.64, -29.76) * mm, "end": v(-10.8, -10.42) * mm});
            skArc(sketch, "E90.0.1", {"start": v(-10.8, -10.42) * mm, "mid": v(-13, -7.5) * mm, "end": v(-14.42, -4.14) * mm});
            skLineSegment(sketch, "E90.0.2", {"start": v(-14.42, -4.14) * mm, "end": v(-42.59, -14.25) * mm});
            skArc(sketch, "E90.0.3", {"start": v(-42.59, -14.25) * mm, "mid": v(-38.9, -22.46) * mm, "end": v(-33.64, -29.76) * mm});
            skLineSegment(sketch, "E91.0.0", {"start": v(-42.59, 14.25) * mm, "end": v(-14.42, 4.14) * mm});
            skArc(sketch, "E91.0.1", {"start": v(-14.42, 4.14) * mm, "mid": v(-13, 7.5) * mm, "end": v(-10.8, 10.42) * mm});
            skLineSegment(sketch, "E91.0.2", {"start": v(-10.8, 10.42) * mm, "end": v(-33.64, 29.76) * mm});
            skArc(sketch, "E91.0.3", {"start": v(-33.64, 29.76) * mm, "mid": v(-38.9, 22.46) * mm, "end": v(-42.59, 14.25) * mm});
            skLineSegment(sketch, "E92.0.0", {"start": v(-8.95, 44.01) * mm, "end": v(-3.63, 14.55) * mm});
            skArc(sketch, "E92.0.1", {"start": v(-3.63, 14.55) * mm, "mid": v(0, 15) * mm, "end": v(3.63, 14.55) * mm});
            skLineSegment(sketch, "E92.0.2", {"start": v(3.63, 14.55) * mm, "end": v(8.95, 44.01) * mm});
            skArc(sketch, "E92.0.3", {"start": v(8.95, 44.01) * mm, "mid": v(0, 44.91) * mm, "end": v(-8.95, 44.01) * mm});
            skLineSegment(sketch, "E93.0.0", {"start": v(33.64, 29.76) * mm, "end": v(10.8, 10.42) * mm});
            skArc(sketch, "E93.0.1", {"start": v(10.8, 10.42) * mm, "mid": v(13, 7.5) * mm, "end": v(14.42, 4.14) * mm});
            skLineSegment(sketch, "E93.0.2", {"start": v(14.42, 4.14) * mm, "end": v(42.59, 14.25) * mm});
            skArc(sketch, "E93.0.3", {"start": v(42.59, 14.25) * mm, "mid": v(38.9, 22.46) * mm, "end": v(33.64, 29.76) * mm});
            skLineSegment(sketch, "E94.0.0", {"start": v(42.59, -14.25) * mm, "end": v(14.42, -4.14) * mm});
            skArc(sketch, "E94.0.1", {"start": v(14.42, -4.14) * mm, "mid": v(13, -7.5) * mm, "end": v(10.8, -10.42) * mm});
            skLineSegment(sketch, "E94.0.2", {"start": v(10.8, -10.42) * mm, "end": v(33.64, -29.76) * mm});
            skArc(sketch, "E94.0.3", {"start": v(33.64, -29.76) * mm, "mid": v(38.9, -22.46) * mm, "end": v(42.59, -14.25) * mm});
            skLineSegment(sketch, "E95.0.0", {"start": v(8.95, -44.01) * mm, "end": v(3.63, -14.55) * mm});
            skArc(sketch, "E95.0.1", {"start": v(3.63, -14.55) * mm, "mid": v(0, -15) * mm, "end": v(-3.63, -14.55) * mm});
            skLineSegment(sketch, "E95.0.2", {"start": v(-3.63, -14.55) * mm, "end": v(-8.95, -44.01) * mm});
            skArc(sketch, "E95.0.3", {"start": v(-8.95, -44.01) * mm, "mid": v(0, -44.91) * mm, "end": v(8.95, -44.01) * mm});
            skCircle(sketch, "E96.0", {"center": v(0, 0) * mm, "radius": 10 * mm});
            skCircle(sketch, "E97.0", {"center": v(0, 0) * mm, "radius": 15 * mm});
            skCircle(sketch, "E98.0", {"center": v(0, 0) * mm, "radius": 8 * mm});
            skCircle(sketch, "E99.0", {"center": v(0, 0) * mm, "radius": 5 * mm});
            skSolve(sketch);
        }
        {
            var Q0;
            Q0=makeQuery(id+"F18.imprint","IMPRINT",FACE,{"disambiguationData":[TD([[makeQuery(id+"F18.imprint","IMPRINT",EDGE,{"derivedFrom":sQuery(id+"F18.wireOp",EDGE,"E89.0")}),1.0]])]});
            var Q1;
            {var subQ0=sQuery(id+"F18.wireOp",EDGE,"E95.0.0");Q1=makeQuery(id+"F18.imprint","IMPRINT",FACE,{"disambiguationData":[TD([[makeQuery(id+"F18.imprint","IMPRINT",EDGE,{"derivedFrom":subQ0}),1.0]])]});}
            var Q2;
            {var subQ0=sQuery(id+"F18.wireOp",EDGE,"E90.0.0");Q2=makeQuery(id+"F18.imprint","IMPRINT",FACE,{"disambiguationData":[TD([[makeQuery(id+"F18.imprint","IMPRINT",EDGE,{"derivedFrom":subQ0}),1.0]])]});}
            var Q3;
            {var subQ0=sQuery(id+"F18.wireOp",EDGE,"E91.0.0");Q3=makeQuery(id+"F18.imprint","IMPRINT",FACE,{"disambiguationData":[TD([[makeQuery(id+"F18.imprint","IMPRINT",EDGE,{"derivedFrom":subQ0}),1.0]])]});}
            var Q4;
            {var subQ0=sQuery(id+"F18.wireOp",EDGE,"E92.0.0");Q4=makeQuery(id+"F18.imprint","IMPRINT",FACE,{"disambiguationData":[TD([[makeQuery(id+"F18.imprint","IMPRINT",EDGE,{"derivedFrom":subQ0}),1.0]])]});}
            var Q5;
            {var subQ0=sQuery(id+"F18.wireOp",EDGE,"E93.0.0");Q5=makeQuery(id+"F18.imprint","IMPRINT",FACE,{"disambiguationData":[TD([[makeQuery(id+"F18.imprint","IMPRINT",EDGE,{"derivedFrom":subQ0}),1.0]])]});}
            var Q6;
            {var subQ0=sQuery(id+"F18.wireOp",EDGE,"E94.0.0");Q6=makeQuery(id+"F18.imprint","IMPRINT",FACE,{"disambiguationData":[TD([[makeQuery(id+"F18.imprint","IMPRINT",EDGE,{"derivedFrom":subQ0}),1.0]])]});}
            var Q7;
            Q7=makeQuery(id+"F18.imprint","IMPRINT",FACE,{"disambiguationData":[TD([[makeQuery(id+"F18.imprint","IMPRINT",EDGE,{"derivedFrom":sQuery(id+"F18.wireOp",EDGE,"E96.0")}),-1.0]])]});
            extrude(context, id + "F19", {"entities" : qUnion([Q0, Q1, Q2, Q3, Q4, Q5, Q6, Q7]), "operationType" : NewBodyOperationType.ADD, "depth" : 5 * mm});
        }
        {
            var Q0;
            Q0=makeQuery(id+"F19.opExtrude","CAP_FACE",FACE,{"disambiguationData":[OSD([sQuery(id+"F18.wireOp",EDGE,"E88.0"),sQuery(id+"F18.wireOp",EDGE,"E89.0"),sQuery(id+"F18.wireOp",EDGE,"E90.0.0"),sQuery(id+"F18.wireOp",EDGE,"E90.0.2"),sQuery(id+"F18.wireOp",EDGE,"E91.0.0"),sQuery(id+"F18.wireOp",EDGE,"E91.0.2"),sQuery(id+"F18.wireOp",EDGE,"E92.0.0"),sQuery(id+"F18.wireOp",EDGE,"E92.0.2"),sQuery(id+"F18.wireOp",EDGE,"E93.0.0"),sQuery(id+"F18.wireOp",EDGE,"E93.0.2"),sQuery(id+"F18.wireOp",EDGE,"E94.0.0"),sQuery(id+"F18.wireOp",EDGE,"E94.0.2"),sQuery(id+"F18.wireOp",EDGE,"E95.0.0"),sQuery(id+"F18.wireOp",EDGE,"E95.0.2"),sQuery(id+"F18.wireOp",EDGE,"E96.0"),sQuery(id+"F18.wireOp",EDGE,"E97.0")])],"isStart":false});
            var sketch = newSketch(context, id + "F20", { "sketchPlane" : qUnion([Q0])});
            skCircle(sketch, "E100.0", {"center": v(0, 0) * mm, "radius": 10 * mm});
            skArc(sketch, "E101.0", {"start": v(-3.63, 14.55) * mm, "mid": v(-7.5, 13) * mm, "end": v(-10.8, 10.42) * mm});
            skCircle(sketch, "E102", {"center": v(0, 0) * mm, "radius": 15 * mm});
            skSolve(sketch);
        }
        {
            var Q0;
            Q0=makeQuery(id+"F20.imprint","IMPRINT",FACE,{"disambiguationData":[TD([[makeQuery(id+"F20.imprint","IMPRINT",EDGE,{"derivedFrom":sQuery(id+"F20.wireOp",EDGE,"E100.0")}),-1.0]])]});
            extrude(context, id + "F21", {"entities" : qUnion([Q0]), "operationType" : NewBodyOperationType.ADD, "depth" : 5 * mm});
        }
        {
            var Q0;
            Q0=makeQuery(id+"F15.imprint","IMPRINT",FACE,{"disambiguationData":[TD([[makeQuery(id+"F15.imprint","IMPRINT",EDGE,{"derivedFrom":sQuery(id+"F15.wireOp",EDGE,"E87")}),1.0]])]});
            var Q1;
            Q1=makeQuery(id+"F9.opPattern","COPY",FACE,{"derivedFrom":makeQuery(id+"F2.opExtrude","CAP_FACE",FACE,{"disambiguationData":[OSD([sQuery(id+"F0.wireOp",EDGE,"E21.0"),sQuery(id+"F0.wireOp",EDGE,"E21.1"),sQuery(id+"F0.wireOp",EDGE,"E21.2"),sQuery(id+"F0.wireOp",EDGE,"E21.3")])],"isStart":false}),"instanceName":"3"});
            extrude(context, id + "F22", {"entities" : qUnion([Q0]), "endBound" : BoundingType.UP_TO_SURFACE, "oppositeDirection" : true, "endBoundEntityFace" : qUnion([Q1]), "depth" : 96.72 * mm});
        }
        {
            var Q0;
            Q0=makeQuery(id+"F0.imprint","IMPRINT",FACE,{"disambiguationData":[TD([[makeQuery(id+"F0.imprint","IMPRINT",EDGE,{"derivedFrom":sQuery(id+"F0.wireOp",EDGE,"E6.0")}),-1.0]])]});
            extrude(context, id + "F23", {"entities" : qUnion([Q0]), "operationType" : NewBodyOperationType.ADD, "depth" : 10 * mm});
        }
        {
            var Q0;
            Q0=makeQuery(id+"F22.opExtrude","CAP_FACE",FACE,{"disambiguationData":[OSD([sQuery(id+"F15.wireOp",EDGE,"E87")])],"isStart":true});
            extrude(context, id + "F24", {"entities" : qUnion([Q0]), "operationType" : NewBodyOperationType.ADD, "depth" : 12.5 * mm});
        }
        {
            var Q0;
            Q0=makeQuery(id+"F24.opExtrude","CAP_FACE",FACE,{"disambiguationData":[OSD([sQuery(id+"F15.wireOp",EDGE,"E87")])],"isStart":false});
            var sketch = newSketch(context, id + "F25", { "sketchPlane" : qUnion([Q0])});
            skCircle(sketch, "E103.0", {"center": v(0, 0) * mm, "radius": 15 * mm});
            skSolve(sketch);
        }
        {
            var Q0;
            Q0=makeQuery(id+"F25.imprint","IMPRINT",FACE,{"disambiguationData":[TD([[makeQuery(id+"F25.imprint","IMPRINT",EDGE,{"derivedFrom":sQuery(id+"F25.wireOp",EDGE,"E103.0")}),1.0]])]});
            var Q1;
            Q1=makeQuery(id+"F25.imprint","IMPRINT",FACE,{"disambiguationData":[TD([[makeQuery(id+"F25.imprint","IMPRINT",EDGE,{"derivedFrom":makeQuery(id+"F24.opExtrude","CAP_EDGE",EDGE,{"disambiguationData":[OSD([sQuery(id+"F15.wireOp",EDGE,"E87")])],"isStart":false})}),1.0]])]});
            var Q2;
            Q2=sQuery(id+"F25.wireOp",EDGE,"E103.0");
            extrude(context, id + "F26", {"entities" : qUnion([Q0, Q1]), "operationType" : NewBodyOperationType.ADD, "surfaceEntities" : qUnion([Q2]), "depth" : 15 * mm});
        }
        {
            var Q0;
            Q0=makeQuery(id+"F26.opExtrude","CAP_FACE",FACE,{"disambiguationData":[OSD([sQuery(id+"F25.wireOp",EDGE,"E103.0")])],"isStart":false});
            var sketch = newSketch(context, id + "F27", { "sketchPlane" : qUnion([Q0])});
            skLineSegment(sketch, "E104.bottom", {"start": v(2.5, 2.5) * mm, "end": v(-2.5, 2.5) * mm});
            skLineSegment(sketch, "E104.top", {"start": v(2.5, -2.5) * mm, "end": v(-2.5, -2.5) * mm});
            skLineSegment(sketch, "E104.left", {"start": v(2.5, 2.5) * mm, "end": v(2.5, -2.5) * mm});
            skLineSegment(sketch, "E104.right", {"start": v(-2.5, 2.5) * mm, "end": v(-2.5, -2.5) * mm});
            skPoint(sketch, "E104.middle", {"position": v(0, 0) * mm});
            skCircle(sketch, "E105", {"center": v(0, 0) * mm, "radius": 7.5 * mm});
            skLineSegment(sketch, "E106.0", {"start": v(2.9, 2.9) * mm, "end": v(-2.9, 2.9) * mm});
            skLineSegment(sketch, "E106.1", {"start": v(2.9, 2.9) * mm, "end": v(2.9, -2.9) * mm});
            skLineSegment(sketch, "E106.2", {"start": v(2.9, -2.9) * mm, "end": v(-2.9, -2.9) * mm});
            skLineSegment(sketch, "E106.3", {"start": v(-2.9, 2.9) * mm, "end": v(-2.9, -2.9) * mm});
            skSolve(sketch);
        }
        {
            var Q0;
            Q0=makeQuery(id+"F27.imprint","IMPRINT",FACE,{"disambiguationData":[TD([[makeQuery(id+"F27.imprint","IMPRINT",EDGE,{"derivedFrom":sQuery(id+"F27.wireOp",EDGE,"E104.bottom")}),1.0]])]});
            extrude(context, id + "F28", {"entities" : qUnion([Q0]), "operationType" : NewBodyOperationType.ADD, "depth" : 10 * mm});
        }
        {
            var Q0;
            Q0=makeQuery(id+"F27.imprint","IMPRINT",FACE,{"disambiguationData":[TD([[makeQuery(id+"F27.imprint","IMPRINT",EDGE,{"derivedFrom":sQuery(id+"F27.wireOp",EDGE,"E105")}),1.0]])]});
            extrude(context, id + "F29", {"entities" : qUnion([Q0]), "depth" : 11.14 * mm});
        }
        {
            var Q0;
            Q0=makeQuery(id+"F29.opExtrude","CAP_FACE",FACE,{"disambiguationData":[OSD([sQuery(id+"F27.wireOp",EDGE,"E105"),sQuery(id+"F27.wireOp",EDGE,"E106.0"),sQuery(id+"F27.wireOp",EDGE,"E106.1"),sQuery(id+"F27.wireOp",EDGE,"E106.2"),sQuery(id+"F27.wireOp",EDGE,"E106.3")])],"isStart":false});
            var sketch = newSketch(context, id + "F30", { "sketchPlane" : qUnion([Q0])});
            skLineSegment(sketch, "E107.0", {"start": v(-2.9, 2.9) * mm, "end": v(-2.9, -2.9) * mm});
            skLineSegment(sketch, "E108.0", {"start": v(2.9, 2.9) * mm, "end": v(-2.9, 2.9) * mm});
            skLineSegment(sketch, "E109.0", {"start": v(2.9, 2.9) * mm, "end": v(2.9, -2.9) * mm});
            skLineSegment(sketch, "E110.0", {"start": v(2.9, -2.9) * mm, "end": v(-2.9, -2.9) * mm});
            skSolve(sketch);
        }
        {
            var Q0;
            Q0=makeQuery(id+"F30.imprint","IMPRINT",FACE,{"disambiguationData":[TD([[makeQuery(id+"F30.imprint","IMPRINT",EDGE,{"derivedFrom":sQuery(id+"F30.wireOp",EDGE,"E107.0")}),1.0]])]});
            var Q1;
            Q1=makeQuery(id+"F30.imprint","IMPRINT",FACE,{"disambiguationData":[TD([[makeQuery(id+"F30.imprint","IMPRINT",EDGE,{"derivedFrom":sQuery(id+"F30.wireOp",EDGE,"E107.0")}),-1.0]])]});
            extrude(context, id + "F31", {"entities" : qUnion([Q0, Q1]), "operationType" : NewBodyOperationType.ADD, "depth" : 120 * mm});
        }
        {
            var Q0;
            Q0=qCreatedBy(makeId("Right.planeOp"),FACE);
            var sketch = newSketch(context, id + "F32", { "sketchPlane" : qUnion([Q0])});
            skLineSegment(sketch, "E111.0", {"start": v(-59.91, 97) * mm, "end": v(59.91, 97) * mm});
            skLineSegment(sketch, "E112", {"start": v(0, 97) * mm, "end": v(0, 167) * mm});
            skPoint(sketch, "E112.endSnap0", {"position": v(0, 97) * mm});
            skSolve(sketch);
        }
        {
            var Q0;
            Q0=sQuery(id+"F32.wireOp",EDGE,"E112");
            var Q1;
            Q1=sQuery(id+"F32.wireOp",VERTEX,"E112.end");
            cPlane(context, id + "F33", {"entities" : qUnion([Q0, Q1]), "cplaneType" : CPlaneType.LINE_POINT, "offset" : 25 * mm, "width" : 150 * mm, "height" : 150 * mm});
        }
        {
            var Q0;
            Q0=qCreatedBy(id+"F33.planeOp",FACE);
            var sketch = newSketch(context, id + "F34", { "sketchPlane" : qUnion([Q0])});
            skCircle(sketch, "E113.0", {"center": v(0, 0) * mm, "radius": 7.5 * mm});
            skCircle(sketch, "E114.0", {"center": v(0, 0) * mm, "radius": 8 * mm});
            skCircle(sketch, "E115.0", {"center": v(0, 0) * mm, "radius": 15 * mm});
            skLineSegment(sketch, "E116", {"start": v(0, 18.17) * mm, "end": v(0, 0) * mm, "construction": true});
            skLineSegment(sketch, "E117.0", {"start": v(-8.95, 44.01) * mm, "end": v(-3.63, 14.55) * mm, "construction": true});
            skLineSegment(sketch, "E118.0", {"start": v(3.63, 14.55) * mm, "end": v(8.95, 44.01) * mm, "construction": true});
            skLineSegment(sketch, "E119", {"start": v(-3.63, 14.55) * mm, "end": v(-2.9, 10.52) * mm});
            skLineSegment(sketch, "E120", {"start": v(-2.9, 10.52) * mm, "end": v(0, 10.52) * mm});
            skLineSegment(sketch, "E121.MirrorCS", {"start": v(2.9, 10.52) * mm, "end": v(0, 10.52) * mm});
            skLineSegment(sketch, "E122.MirrorCS", {"start": v(3.63, 14.55) * mm, "end": v(2.9, 10.52) * mm});
            skLineSegment(sketch, "E123.1.0", {"start": v(-14.42, -4.14) * mm, "end": v(-10.56, -2.75) * mm});
            skLineSegment(sketch, "E123.1.1", {"start": v(-10.56, -2.75) * mm, "end": v(-9.11, -5.26) * mm});
            skLineSegment(sketch, "E123.1.2", {"start": v(-10.8, -10.42) * mm, "end": v(-7.66, -7.77) * mm});
            skLineSegment(sketch, "E123.1.3", {"start": v(-7.66, -7.77) * mm, "end": v(-9.11, -5.26) * mm});
            skLineSegment(sketch, "E123.2.0", {"start": v(10.8, -10.42) * mm, "end": v(7.66, -7.77) * mm});
            skLineSegment(sketch, "E123.2.1", {"start": v(7.66, -7.77) * mm, "end": v(9.11, -5.26) * mm});
            skLineSegment(sketch, "E123.2.2", {"start": v(14.42, -4.14) * mm, "end": v(10.56, -2.75) * mm});
            skLineSegment(sketch, "E123.2.3", {"start": v(10.56, -2.75) * mm, "end": v(9.11, -5.26) * mm});
            skSolve(sketch);
        }
        {
            var Q0;
            Q0=makeQuery(id+"F19.opExtrude","CAP_FACE",FACE,{"disambiguationData":[OSD([sQuery(id+"F18.wireOp",EDGE,"E88.0"),sQuery(id+"F18.wireOp",EDGE,"E89.0"),sQuery(id+"F18.wireOp",EDGE,"E90.0.0"),sQuery(id+"F18.wireOp",EDGE,"E90.0.2"),sQuery(id+"F18.wireOp",EDGE,"E91.0.0"),sQuery(id+"F18.wireOp",EDGE,"E91.0.2"),sQuery(id+"F18.wireOp",EDGE,"E92.0.0"),sQuery(id+"F18.wireOp",EDGE,"E92.0.2"),sQuery(id+"F18.wireOp",EDGE,"E93.0.0"),sQuery(id+"F18.wireOp",EDGE,"E93.0.2"),sQuery(id+"F18.wireOp",EDGE,"E94.0.0"),sQuery(id+"F18.wireOp",EDGE,"E94.0.2"),sQuery(id+"F18.wireOp",EDGE,"E95.0.0"),sQuery(id+"F18.wireOp",EDGE,"E95.0.2"),sQuery(id+"F18.wireOp",EDGE,"E96.0"),sQuery(id+"F18.wireOp",EDGE,"E97.0")])],"isStart":false});
            var sketch = newSketch(context, id + "F35", { "sketchPlane" : qUnion([Q0])});
            skLineSegment(sketch, "E124", {"start": v(0, 0) * mm, "end": v(0, 62.8) * mm, "construction": true});
            skPoint(sketch, "E124.endSnap0", {"position": v(0, 15) * mm});
            skLineSegment(sketch, "E125", {"start": v(-8.37, 59.32) * mm, "end": v(-6.54, 49.23) * mm});
            skLineSegment(sketch, "E126", {"start": v(-6.54, 49.23) * mm, "end": v(0, 49.23) * mm});
            skLineSegment(sketch, "E127.MirrorCS", {"start": v(6.54, 49.23) * mm, "end": v(0, 49.23) * mm});
            skLineSegment(sketch, "E128.MirrorCS", {"start": v(8.37, 59.32) * mm, "end": v(6.54, 49.23) * mm});
            skLineSegment(sketch, "E129.1.0", {"start": v(-55.56, -22.42) * mm, "end": v(-45.9, -18.95) * mm});
            skLineSegment(sketch, "E129.1.1", {"start": v(-45.9, -18.95) * mm, "end": v(-42.64, -24.62) * mm});
            skLineSegment(sketch, "E129.1.2", {"start": v(-39.37, -30.28) * mm, "end": v(-42.64, -24.62) * mm});
            skLineSegment(sketch, "E129.1.3", {"start": v(-47.2, -36.9) * mm, "end": v(-39.37, -30.28) * mm});
            skLineSegment(sketch, "E129.2.0", {"start": v(47.2, -36.9) * mm, "end": v(39.37, -30.28) * mm});
            skLineSegment(sketch, "E129.2.1", {"start": v(39.37, -30.28) * mm, "end": v(42.64, -24.62) * mm});
            skLineSegment(sketch, "E129.2.2", {"start": v(45.9, -18.95) * mm, "end": v(42.64, -24.62) * mm});
            skLineSegment(sketch, "E129.2.3", {"start": v(55.56, -22.42) * mm, "end": v(45.9, -18.95) * mm});
            skPoint(sketch, "E129.center", {"position": v(0, 0) * mm});
            skSolve(sketch);
        }
        {
            var Q1;
            {var subQ1=sQuery(id+"F34.wireOp",EDGE,"E123.1.0");Q1=makeQuery(id+"F34.imprint","IMPRINT",FACE,{"disambiguationData":[TD([[makeQuery(id+"F34.imprint","IMPRINT",EDGE,{"derivedFrom":subQ1}),-1.0]])]});}
            var Q2;
            {var subQ4=sQuery(id+"F35.wireOp",EDGE,"E129.1.1");Q2=makeQuery(id+"F35.imprint","IMPRINT",FACE,{"disambiguationData":[TD([[makeQuery(id+"F35.imprint","IMPRINT",EDGE,{"derivedFrom":subQ4}),-1.0]])]});}
            loft(context, id + "F36", {"operationType" : NewBodyOperationType.ADD, "sheetProfilesArray" : [{ "sheetProfileEntities" : qUnion([Q1]) }, { "sheetProfileEntities" : qUnion([Q2]) }]});
        }
        {
            var Q1;
            {var subQ1=sQuery(id+"F34.wireOp",EDGE,"E123.2.0");Q1=makeQuery(id+"F34.imprint","IMPRINT",FACE,{"disambiguationData":[TD([[makeQuery(id+"F34.imprint","IMPRINT",EDGE,{"derivedFrom":subQ1}),-1.0]])]});}
            var Q2;
            {var subQ4=sQuery(id+"F35.wireOp",EDGE,"E129.2.1");Q2=makeQuery(id+"F35.imprint","IMPRINT",FACE,{"disambiguationData":[TD([[makeQuery(id+"F35.imprint","IMPRINT",EDGE,{"derivedFrom":subQ4}),-1.0]])]});}
            loft(context, id + "F37", {"operationType" : NewBodyOperationType.ADD, "sheetProfilesArray" : [{ "sheetProfileEntities" : qUnion([Q1]) }, { "sheetProfileEntities" : qUnion([Q2]) }]});
        }
        {
            var Q1;
            {var subQ0=sQuery(id+"F34.wireOp",EDGE,"E119");Q1=makeQuery(id+"F34.imprint","IMPRINT",FACE,{"disambiguationData":[TD([[makeQuery(id+"F34.imprint","IMPRINT",EDGE,{"derivedFrom":subQ0}),1.0]])]});}
            var Q2;
            {var subQ1=sQuery(id+"F35.wireOp",EDGE,"E125");Q2=makeQuery(id+"F35.imprint","IMPRINT",FACE,{"disambiguationData":[TD([[makeQuery(id+"F35.imprint","IMPRINT",EDGE,{"derivedFrom":subQ1}),1.0]])]});}
            loft(context, id + "F38", {"operationType" : NewBodyOperationType.ADD, "sheetProfilesArray" : [{ "sheetProfileEntities" : qUnion([Q1]) }, { "sheetProfileEntities" : qUnion([Q2]) }]});
        }
        {
            var Q0;
            Q0=makeQuery(id+"F34.imprint","IMPRINT",FACE,{"disambiguationData":[TD([[makeQuery(id+"F34.imprint","IMPRINT",EDGE,{"derivedFrom":sQuery(id+"F34.wireOp",EDGE,"E114.0")}),-1.0]])]});
            var Q1;
            {var subQ1=sQuery(id+"F34.wireOp",EDGE,"E123.1.0");Q1=makeQuery(id+"F34.imprint","IMPRINT",FACE,{"disambiguationData":[TD([[makeQuery(id+"F34.imprint","IMPRINT",EDGE,{"derivedFrom":subQ1}),-1.0]])]});}
            var Q2;
            {var subQ1=sQuery(id+"F34.wireOp",EDGE,"E123.2.0");Q2=makeQuery(id+"F34.imprint","IMPRINT",FACE,{"disambiguationData":[TD([[makeQuery(id+"F34.imprint","IMPRINT",EDGE,{"derivedFrom":subQ1}),-1.0]])]});}
            var Q3;
            {var subQ0=sQuery(id+"F34.wireOp",EDGE,"E119");Q3=makeQuery(id+"F34.imprint","IMPRINT",FACE,{"disambiguationData":[TD([[makeQuery(id+"F34.imprint","IMPRINT",EDGE,{"derivedFrom":subQ0}),1.0]])]});}
            extrude(context, id + "F39", {"entities" : qUnion([Q0, Q1, Q2, Q3]), "operationType" : NewBodyOperationType.ADD, "depth" : 5 * mm});
        }
        {
            var Q0;
            Q0=qCreatedBy(makeId("Right.planeOp"),FACE);
            var sketch = newSketch(context, id + "F40", { "sketchPlane" : qUnion([Q0])});
            skLineSegment(sketch, "E130.0", {"start": v(-7.5, 248.64) * mm, "end": v(7.5, 248.64) * mm});
            skLineSegment(sketch, "E131", {"start": v(0, 248.64) * mm, "end": v(0, 258.64) * mm});
            skSolve(sketch);
        }
        {
            var Q0;
            Q0=sQuery(id+"F40.wireOp",EDGE,"E131");
            var Q1;
            Q1=sQuery(id+"F40.wireOp",VERTEX,"E131.end");
            cPlane(context, id + "F41", {"entities" : qUnion([Q0, Q1]), "cplaneType" : CPlaneType.LINE_POINT, "offset" : 25 * mm, "width" : 150 * mm, "height" : 150 * mm});
        }
        {
            var Q0;
            Q0=qCreatedBy(id+"F41.planeOp",FACE);
            var sketch = newSketch(context, id + "F42", { "sketchPlane" : qUnion([Q0])});
            skCircle(sketch, "E132", {"center": v(0, 0) * mm, "radius": 2 * mm});
            skSolve(sketch);
        }
        {
            var Q1;
            Q1=makeQuery(id+"F42.imprint","IMPRINT",FACE,{"disambiguationData":[TD([[makeQuery(id+"F42.imprint","IMPRINT",EDGE,{"derivedFrom":sQuery(id+"F42.wireOp",EDGE,"E132")}),1.0]])]});
            var Q2;
            Q2=makeQuery(id+"F31.opExtrude","CAP_FACE",FACE,{"disambiguationData":[OSD([sQuery(id+"F27.wireOp",EDGE,"E105")])],"isStart":false});
            loft(context, id + "F43", {"operationType" : NewBodyOperationType.ADD, "sheetProfilesArray" : [{ "sheetProfileEntities" : qUnion([Q1]) }, { "sheetProfileEntities" : qUnion([Q2]) }]});
        }
    });
